# Revit family: STH7925_30
name_source: partatom
category: Luminárias
units: mm (PartAtom-declared; Revit-internal decimal feet)

## family parameters
Compartilhado = Não
Corte com vazios quando carregada = Não
Cota do conector redondo = Utilizar diâmetro
Fonte luminosa = Sim
Hospedeiro = Forro
Manter orientação da anotação = Não
Número OmniClass = 23.80.70.11
Ponto de cálculo do ambiente = Não
Sempre na vertical = Sim
Tipo de parte = Normal
Título OmniClass = Luminaries for Internal Lighting

## types (1)
- STH7925/30 - BRANCO - BIVOLT - 3000K - 1000lm - 30°
    Altura = 0.06 m
    Arquivo de rede fotométrica = STELLA - STH7925-30 - EASY PAR30.ies
    Comprimento = 0.14 m
    Cromado = Cromado
    Dimerização = Não dimerizável
    Elevação padrão = 0 m
    Estrutura = Al - Branco
    Fabricante = Stella
    Filtro de cor = 16777215
    Fluxo Luminoso = 1000 lm
    Grau de proteção (IP) = IP20
    IRC (Índice de reprodução de cores) = >80
    Largura = 0.14 m
    Luminoso = Luminoso - 3000K
    Modelo = Easy PAR30
    Potência = 12 W
    Referência = STH7925/30 - BRANCO
    Temperatura da cor (K) = 3000 K
    Tensão Elétrica = 100V-240V
    Troca de temperatura da cor de lâmpada com esmaecimento = <Nenhum>
    URL = https://stella.com.br
    Vidro = Vidro
    Ângulo de Abertura = 30°
    Ângulo de inclinação = 90.00°
